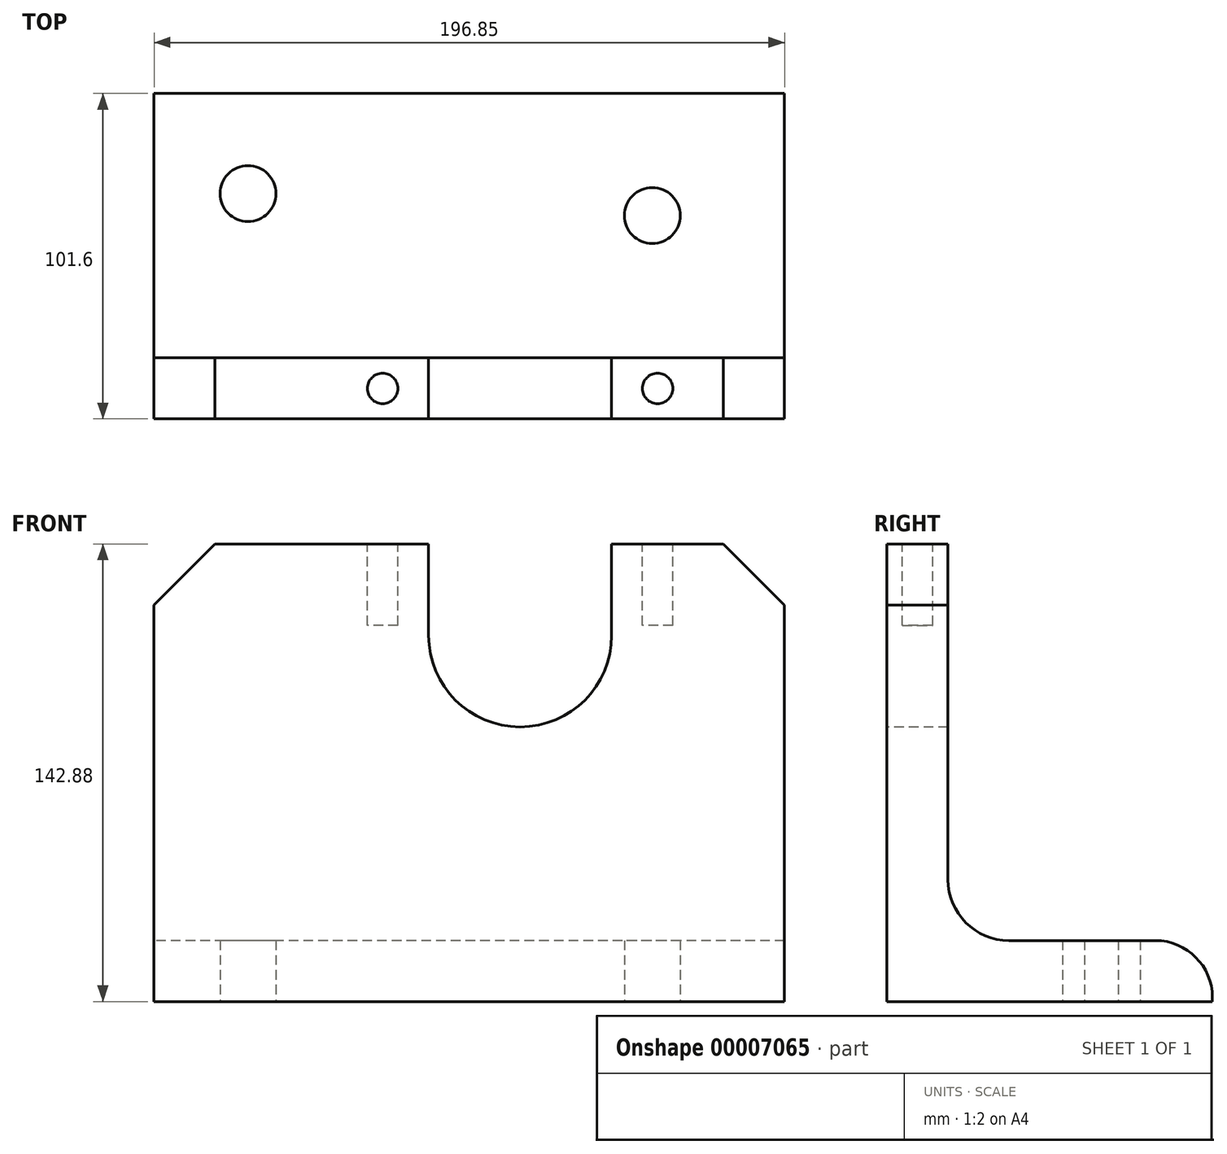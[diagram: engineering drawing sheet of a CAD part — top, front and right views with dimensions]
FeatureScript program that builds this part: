
annotation { "Feature Type Name" : "Feature", "Feature Type Description" : "" }
export const myFeature = defineFeature(function(context is Context, id is Id, definition is map)
    precondition{}
    {
        {
            var Q0;
            Q0=qCreatedBy(makeId("Right.planeOp"),FACE);
            var sketch = newSketch(context, id + "F0", { "sketchPlane" : qUnion([Q0])});
            skLineSegment(sketch, "E0", {"start": v(0, 0) * mm, "end": v(0, 142.88) * mm});
            skLineSegment(sketch, "E1", {"start": v(0, 0) * mm, "end": v(101.6, 0) * mm});
            skLineSegment(sketch, "E2.0", {"start": v(19.05, 38.1) * mm, "end": v(19.05, 142.88) * mm});
            skLineSegment(sketch, "E3.0", {"start": v(38.1, 19.05) * mm, "end": v(83.82, 19.05) * mm});
            skArc(sketch, "E4.filletArc", {"start": v(19.05, 38.1) * mm, "mid": v(24.63, 24.63) * mm, "end": v(38.1, 19.05) * mm});
            skLineSegment(sketch, "E5", {"start": v(101.6, 0) * mm, "end": v(101.6, 1.27) * mm});
            skPoint(sketch, "E6.visualSharp", {"position": v(101.6, 19.05) * mm});
            skArc(sketch, "E6.filletArc", {"start": v(101.6, 1.27) * mm, "mid": v(96.4, 13.84) * mm, "end": v(83.82, 19.05) * mm});
            skLineSegment(sketch, "E7", {"start": v(0, 142.88) * mm, "end": v(19.05, 142.88) * mm});
            skSolve(sketch);
        }
        {
            var Q0;
            Q0=makeQuery(id+"F0.imprint","IMPRINT",FACE,{"disambiguationData":[TD([[makeQuery(id+"F0.imprint","IMPRINT",EDGE,{"derivedFrom":sQuery(id+"F0.wireOp",EDGE,"E0")}),-1.0]])]});
            extrude(context, id + "F1", {"entities" : qUnion([Q0]), "endBound" : BoundingType.SYMMETRIC, "depth" : 196.85 * mm});
        }
        {
            var Q0;
            Q0=makeQuery(id+"F1.opExtrude","SWEPT_FACE",FACE,{"disambiguationData":[OSD([sQuery(id+"F0.wireOp",EDGE,"E0")])]});
            var sketch = newSketch(context, id + "F2", { "sketchPlane" : qUnion([Q0])});
            skLineSegment(sketch, "E8.0", {"start": v(15.88, 0) * mm, "end": v(15.88, 142.88) * mm, "construction": true});
            skLineSegment(sketch, "E9.0", {"start": v(98.43, 114.3) * mm, "end": v(-98.43, 114.3) * mm, "construction": true});
            skArc(sketch, "E10", {"start": v(-12.7, 114.3) * mm, "mid": v(15.87, 85.73) * mm, "end": v(44.45, 114.3) * mm});
            skLineSegment(sketch, "E11", {"start": v(-12.7, 114.3) * mm, "end": v(-12.7, 176.83) * mm});
            skLineSegment(sketch, "E12", {"start": v(44.45, 114.3) * mm, "end": v(44.45, 176.83) * mm});
            skLineSegment(sketch, "E13", {"start": v(44.45, 176.83) * mm, "end": v(-12.7, 176.83) * mm});
            skSolve(sketch);
        }
        {
            var Q0;
            Q0 = qSketchRegion(id + "F2", true);
            extrude(context, id + "F3", {"entities" : qUnion([Q0]), "operationType" : NewBodyOperationType.REMOVE, "endBound" : BoundingType.THROUGH_ALL, "oppositeDirection" : true, "depth" : 25.4 * mm});
        }
        {
            var Q0;
            Q0=makeQuery(id+"F1.opExtrude","CAP_EDGE",EDGE,{"disambiguationData":[OSD([sQuery(id+"F0.wireOp",EDGE,"E7")])],"isStart":true});
            var Q1;
            Q1=makeQuery(id+"F1.opExtrude","CAP_EDGE",EDGE,{"disambiguationData":[OSD([sQuery(id+"F0.wireOp",EDGE,"E7")])],"isStart":false});
            chamfer(context, id + "F4", {"entities" : qUnion([Q0, Q1]), "width" : 19.05 * mm, "tangentPropagation" : true});
        }
        {
            var Q0;
            {var subQ0=sQuery(id+"F0.wireOp",EDGE,"E7");Q0=makeQuery(id+"F3.boolean.opBoolean","SPLIT",FACE,{"disambiguationData":[TD([makeQuery(id+"F3.opExtrude","SWEPT_FACE",FACE,{"disambiguationData":[OSD([sQuery(id+"F2.wireOp",EDGE,"E11")])]})])],"derivedFrom":makeQuery(id+"F1.opExtrude","SWEPT_FACE",FACE,{"disambiguationData":[OSD([subQ0])]})});}
            var sketch = newSketch(context, id + "F5", { "sketchPlane" : qUnion([Q0])});
            skLineSegment(sketch, "E14.0", {"start": v(-12.7, 19.05) * mm, "end": v(-12.7, 0) * mm, "construction": true});
            skLineSegment(sketch, "E15.0", {"start": v(44.45, 0) * mm, "end": v(44.45, 19.05) * mm, "construction": true});
            skLineSegment(sketch, "E16", {"start": v(-12.7, 9.53) * mm, "end": v(44.45, 9.53) * mm, "construction": true});
            skLineSegment(sketch, "E17", {"start": v(15.88, 9.53) * mm, "end": v(15.88, -21.65) * mm, "construction": true});
            skLineSegment(sketch, "E18.0", {"start": v(-27.05, 9.52) * mm, "end": v(-27.05, -21.65) * mm, "construction": true});
            skLineSegment(sketch, "E19.0", {"start": v(58.8, 9.53) * mm, "end": v(58.8, -21.65) * mm, "construction": true});
            skCircle(sketch, "E20", {"center": v(-27.05, 9.52) * mm, "radius": 4.76 * mm});
            skCircle(sketch, "E21.0.MirrorC", {"center": v(58.8, 9.52) * mm, "radius": 4.76 * mm});
            skSolve(sketch);
        }
        {
            var Q0;
            Q0 = qSketchRegion(id + "F5", true);
            extrude(context, id + "F6", {"entities" : qUnion([Q0]), "operationType" : NewBodyOperationType.REMOVE, "oppositeDirection" : true, "depth" : 25.4 * mm});
        }
        {
            var Q0;
            Q0=makeQuery(id+"F1.opExtrude","SWEPT_FACE",FACE,{"disambiguationData":[OSD([sQuery(id+"F0.wireOp",EDGE,"E1")])]});
            var sketch = newSketch(context, id + "F7", { "sketchPlane" : qUnion([Q0])});
            skLineSegment(sketch, "E22.0", {"start": v(57.15, 0) * mm, "end": v(57.15, -101.6) * mm, "construction": true});
            skLineSegment(sketch, "E23.0", {"start": v(-69.09, 0) * mm, "end": v(-69.09, -101.6) * mm, "construction": true});
            skLineSegment(sketch, "E24.0", {"start": v(98.43, -70.36) * mm, "end": v(-98.43, -70.36) * mm, "construction": true});
            skCircle(sketch, "E25", {"center": v(-69.09, -70.36) * mm, "radius": 8.73 * mm});
            skLineSegment(sketch, "E26.0", {"start": v(98.43, -63.5) * mm, "end": v(-98.43, -63.5) * mm, "construction": true});
            skCircle(sketch, "E27", {"center": v(57.15, -63.5) * mm, "radius": 8.73 * mm});
            skSolve(sketch);
        }
        {
            var Q0;
            Q0 = qSketchRegion(id + "F7", true);
            extrude(context, id + "F8", {"entities" : qUnion([Q0]), "operationType" : NewBodyOperationType.REMOVE, "endBound" : BoundingType.THROUGH_ALL, "oppositeDirection" : true, "depth" : 25.4 * mm});
        }
    });
